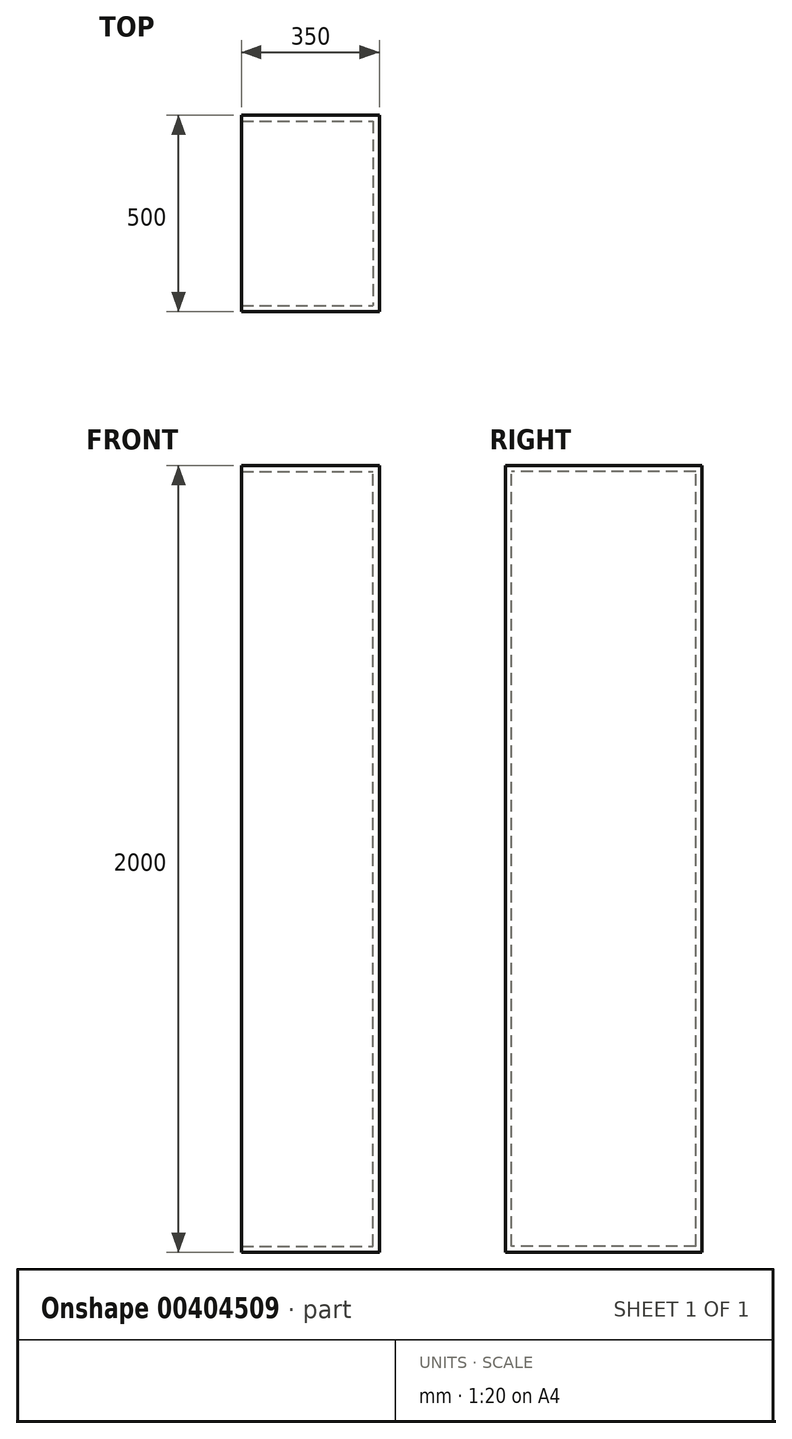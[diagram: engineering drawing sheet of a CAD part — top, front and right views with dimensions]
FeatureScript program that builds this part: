
annotation { "Feature Type Name" : "Feature", "Feature Type Description" : "" }
export const myFeature = defineFeature(function(context is Context, id is Id, definition is map)
    precondition{}
    {
        {
            var Q0;
            Q0=qCreatedBy(makeId("Right.planeOp"),FACE);
            var sketch = newSketch(context, id + "F0", { "sketchPlane" : qUnion([Q0])});
            skLineSegment(sketch, "E0.bottom", {"start": v(0, 0) * mm, "end": v(-45.83, 0) * mm});
            skLineSegment(sketch, "E0.top", {"start": v(0, 53.04) * mm, "end": v(-45.83, 53.04) * mm});
            skLineSegment(sketch, "E0.left", {"start": v(0, 0) * mm, "end": v(0, 53.04) * mm});
            skLineSegment(sketch, "E0.right", {"start": v(-45.83, 0) * mm, "end": v(-45.83, 53.04) * mm});
            skSolve(sketch);
        }
        {
            var Q0;
            Q0=makeQuery(id+"F0.imprint","IMPRINT",FACE,{"disambiguationData":[TD([[makeQuery(id+"F0.imprint","IMPRINT",EDGE,{"derivedFrom":sQuery(id+"F0.wireOp",EDGE,"E0.bottom")}),-1.0]])]});
            extrude(context, id + "F1", {"entities" : qUnion([Q0]), "oppositeDirection" : true, "depth" : 350 * mm});
        }
        {
            var Q0;
            Q0=makeQuery(id+"F1.opExtrude","SWEPT_FACE",FACE,{"disambiguationData":[OSD([sQuery(id+"F0.wireOp",EDGE,"E0.left")])]});
            extrude(context, id + "F2", {"entities" : qUnion([Q0]), "operationType" : NewBodyOperationType.ADD, "oppositeDirection" : true, "depth" : 500 * mm});
        }
        {
            var Q0;
            {var subQ0=sQuery(id+"F0.wireOp",EDGE,"E0.bottom");Q0=makeQuery(id+"F2.boolean.opBoolean","MERGE",FACE,{"derivedFrom":[makeQuery(id+"F1.opExtrude","SWEPT_FACE",FACE,{"disambiguationData":[OSD([subQ0])]}),makeQuery(id+"F2.opExtrude","SWEPT_FACE",FACE,{"disambiguationData":[OSD([subQ0,sQuery(id+"F0.wireOp",EDGE,"E0.left")])]})]});}
            extrude(context, id + "F3", {"entities" : qUnion([Q0]), "operationType" : NewBodyOperationType.ADD, "oppositeDirection" : true, "depth" : 2000 * mm});
        }
        {
            var Q0;
            {var subQ0=sQuery(id+"F0.wireOp",EDGE,"E0.left");var subQ1=sQuery(id+"F0.wireOp",EDGE,"E0.bottom");Q0=makeQuery(id+"F3.boolean.opBoolean","MERGE",FACE,{"derivedFrom":[makeQuery(id+"F2.boolean.opBoolean","MERGE",FACE,{"derivedFrom":[makeQuery(id+"F1.opExtrude","CAP_FACE",FACE,{"disambiguationData":[OSD([subQ1,sQuery(id+"F0.wireOp",EDGE,"E0.top"),subQ0,sQuery(id+"F0.wireOp",EDGE,"E0.right")])],"isStart":false}),makeQuery(id+"F2.opExtrude","SWEPT_FACE",FACE,{"disambiguationData":[OSD([subQ0]),TDD([makeQuery(id+"F1.opExtrude","CAP_EDGE",EDGE,{"disambiguationData":[OSD([subQ0])],"isStart":false})])]})]}),makeQuery(id+"F3.opExtrude","SWEPT_FACE",FACE,{"disambiguationData":[OSD([subQ1,subQ0]),TDD([makeQuery(id+"F2.boolean.opBoolean","MERGE",EDGE,{"derivedFrom":[makeQuery(id+"F1.opExtrude","CAP_EDGE",EDGE,{"disambiguationData":[OSD([subQ1])],"isStart":false}),makeQuery(id+"F2.opExtrude","SWEPT_EDGE",EDGE,{"disambiguationData":[OSD([subQ1,subQ0]),TDD([makeQuery(id+"F1.opExtrude","CAP_VERTEX",VERTEX,{"disambiguationData":[OSD([subQ1,subQ0])],"isStart":false})])]})]})])]})]});}
            shell(context, id + "F4", {"entities" : qUnion([Q0]), "thickness" : 16 * mm});
        }
    });
